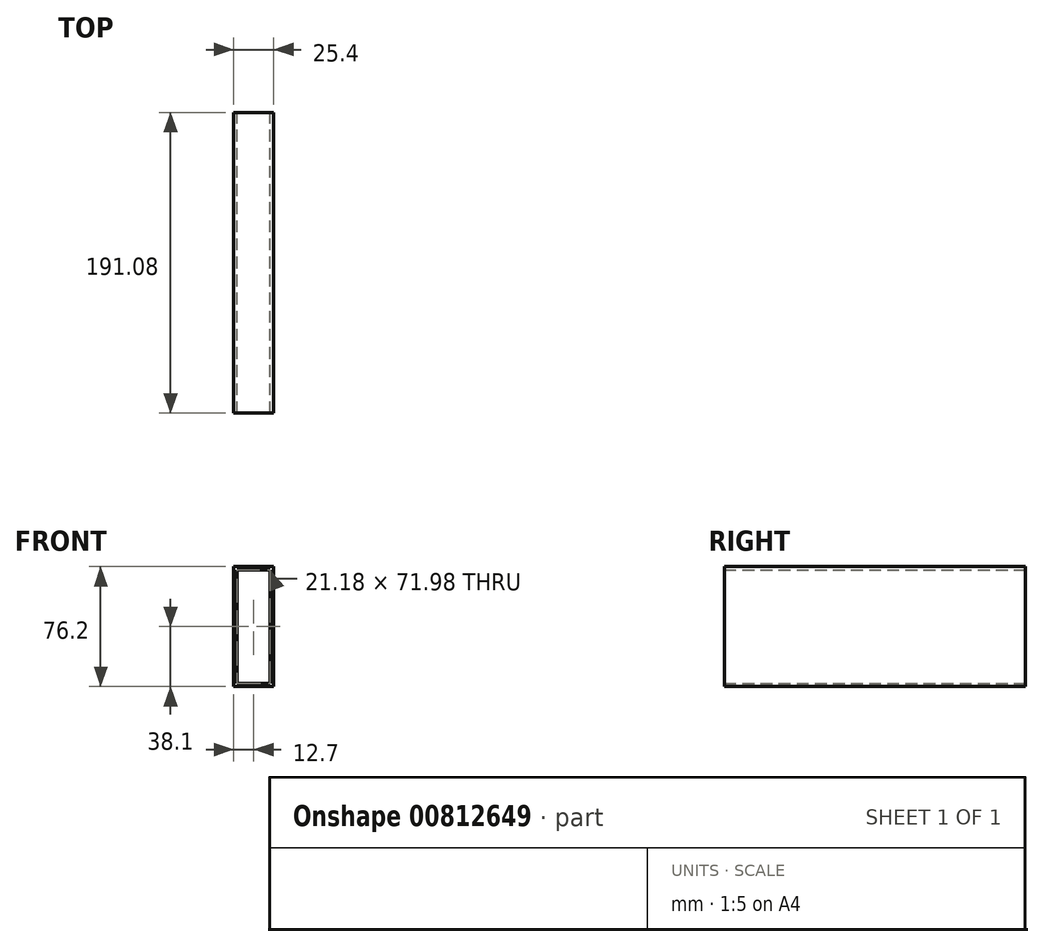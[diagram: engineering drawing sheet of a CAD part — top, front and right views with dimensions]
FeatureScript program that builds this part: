
annotation { "Feature Type Name" : "Feature", "Feature Type Description" : "" }
export const myFeature = defineFeature(function(context is Context, id is Id, definition is map)
    precondition{}
    {
        {
            var Q0;
            Q0=qCreatedBy(makeId("Front.planeOp"),FACE);
            var sketch = newSketch(context, id + "F0", { "sketchPlane" : qUnion([Q0])});
            skLineSegment(sketch, "E0.bottom", {"start": v(12.7, 38.1) * mm, "end": v(-12.7, 38.1) * mm});
            skLineSegment(sketch, "E0.top", {"start": v(12.7, -38.1) * mm, "end": v(-12.7, -38.1) * mm});
            skLineSegment(sketch, "E0.left", {"start": v(12.7, 38.1) * mm, "end": v(12.7, -38.1) * mm});
            skLineSegment(sketch, "E0.right", {"start": v(-12.7, 38.1) * mm, "end": v(-12.7, -38.1) * mm});
            skPoint(sketch, "E0.middle", {"position": v(0, 0) * mm});
            skLineSegment(sketch, "E1.0", {"start": v(10.6, 36) * mm, "end": v(-10.6, 36) * mm});
            skLineSegment(sketch, "E1.1", {"start": v(10.6, 36) * mm, "end": v(10.6, -36) * mm});
            skLineSegment(sketch, "E1.2", {"start": v(10.6, -36) * mm, "end": v(-10.6, -36) * mm});
            skLineSegment(sketch, "E1.3", {"start": v(-10.6, 36) * mm, "end": v(-10.6, -36) * mm});
            skSolve(sketch);
        }
        {
            var Q0;
            Q0=makeQuery(id+"F0.imprint","IMPRINT",FACE,{"disambiguationData":[TD([[makeQuery(id+"F0.imprint","IMPRINT",EDGE,{"derivedFrom":sQuery(id+"F0.wireOp",EDGE,"E0.bottom")}),1.0]])]});
            extrude(context, id + "F1", {"entities" : qUnion([Q0]), "depth" : 191.08 * mm, "offsetDistance" : 25.4 * mm});
        }
    });
